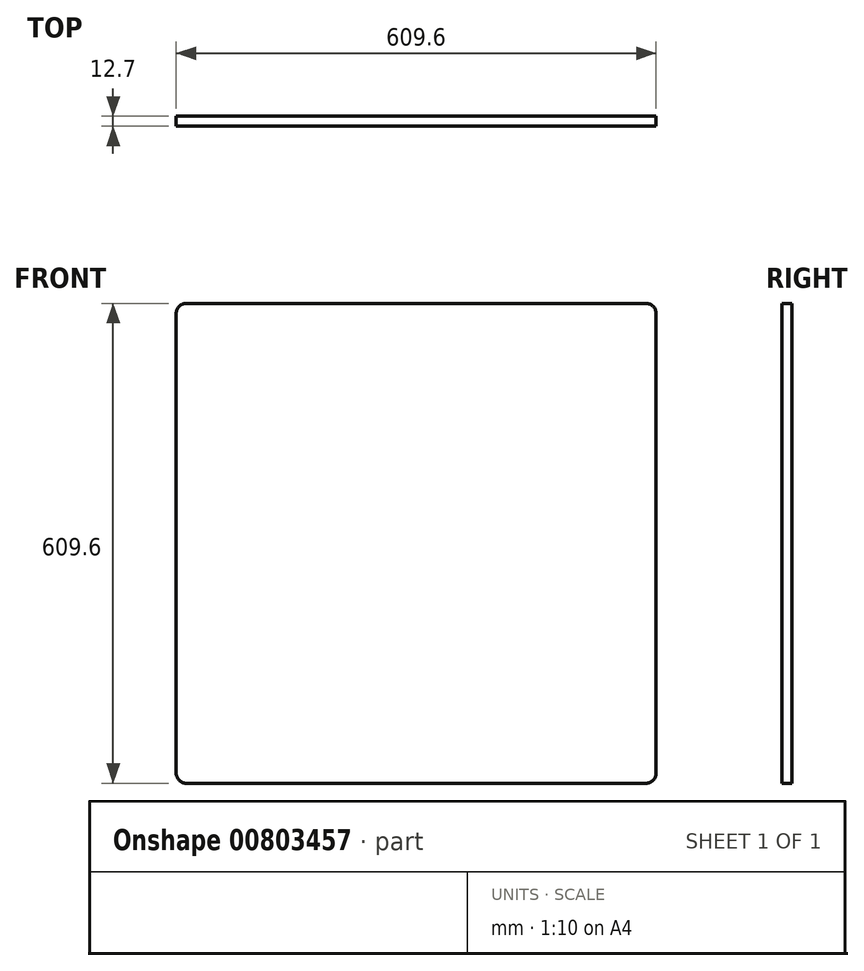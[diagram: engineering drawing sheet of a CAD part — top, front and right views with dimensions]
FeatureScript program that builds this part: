
annotation { "Feature Type Name" : "Feature", "Feature Type Description" : "" }
export const myFeature = defineFeature(function(context is Context, id is Id, definition is map)
    precondition{}
    {
        {
            var Q0;
            Q0=qCreatedBy(makeId("Front.planeOp"),FACE);
            var sketch = newSketch(context, id + "F0", { "sketchPlane" : qUnion([Q0])});
            skLineSegment(sketch, "E0.bottom", {"start": v(-292.1, 304.8) * mm, "end": v(292.1, 304.8) * mm});
            skLineSegment(sketch, "E0.top", {"start": v(-292.1, -304.8) * mm, "end": v(292.1, -304.8) * mm});
            skLineSegment(sketch, "E0.left", {"start": v(-304.8, 292.1) * mm, "end": v(-304.8, -292.1) * mm});
            skLineSegment(sketch, "E0.right", {"start": v(304.8, 292.1) * mm, "end": v(304.8, -292.1) * mm});
            skPoint(sketch, "E0.middle", {"position": v(0, 0) * mm});
            skPoint(sketch, "E1.visualSharp", {"position": v(-304.8, 304.8) * mm});
            skArc(sketch, "E1.filletArc", {"start": v(-292.1, 304.8) * mm, "mid": v(-301.08, 301.08) * mm, "end": v(-304.8, 292.1) * mm});
            skPoint(sketch, "E2.visualSharp", {"position": v(304.8, 304.8) * mm});
            skArc(sketch, "E2.filletArc", {"start": v(304.8, 292.1) * mm, "mid": v(301.08, 301.08) * mm, "end": v(292.1, 304.8) * mm});
            skPoint(sketch, "E3.visualSharp", {"position": v(304.8, -304.8) * mm});
            skArc(sketch, "E3.filletArc", {"start": v(292.1, -304.8) * mm, "mid": v(301.08, -301.08) * mm, "end": v(304.8, -292.1) * mm});
            skPoint(sketch, "E4.visualSharp", {"position": v(-304.8, -304.8) * mm});
            skArc(sketch, "E4.filletArc", {"start": v(-304.8, -292.1) * mm, "mid": v(-301.08, -301.08) * mm, "end": v(-292.1, -304.8) * mm});
            skSolve(sketch);
        }
        {
            var Q0;
            Q0=makeQuery(id+"F0.imprint","IMPRINT",FACE,{"disambiguationData":[TD([[makeQuery(id+"F0.imprint","IMPRINT",EDGE,{"derivedFrom":sQuery(id+"F0.wireOp",EDGE,"E0.bottom")}),-1.0]])]});
            extrude(context, id + "F1", {"entities" : qUnion([Q0]), "endBound" : BoundingType.SYMMETRIC, "depth" : 12.7 * mm, "offsetDistance" : 25.4 * mm});
        }
    });
